# Revit family: ElectricalFixture_WiringAccessories_Hager_Sollysta_RaisedDecorative50ADoublePoleSwitches
name_source: partatom
category: Electrical Fixtures
revit_build: Autodesk Revit 2015 (Build: 20160512_1515(x64)
units: mm (PartAtom-declared; Revit-internal decimal feet)

## types (7) — shared parameters
CE Approval = Yes
Default Elevation = 1219.2 mm  [stored 4 ft]
Design Country = China
Distance From Centre = 22.4 mm
Distance From Edge = 63.6 mm
Double = No
Expected Life = 25 years
Extrusion From Wall = 11.9 mm  [stored 0.039042 ft]
Frequency = 50/60Hz
Gross Weight kg = 0.165
LED Indicator Switch = Yes
Manufacturer = Hager
Manufacturer Country = United Kingdom
Manufacturer Website = http://www.hager.co.uk
Overall Depth = 21.9 mm
Overall Height = 86 mm  [stored 0.282152 ft]
Overall Length = 86 mm  [stored 0.282152 ft]
Overall Width = 86 mm  [stored 0.282152 ft]
Packaging Recyclable = Yes
Product Family = Decorative50ADoublePoleSwitches
Product Group = WiringAccessories
Product Literature = http://www.hager.co.uk
Product Range = Sollysta
Product URL = http://www.hager.co.uk
Reference Standard = BS 1363-2
Shape = Rectangular
Shipping Weight kg = 0.188
Single = Yes
Supply Phase = 1
Switch = Yes
Type = ElectricalFixture
Voltage (Volts) = 230V/240V

## per-type parameters (varying)
| type | Colour | Description | EAN Code | Features | Finish | Material | Name | Technical Description |
| WRDP50NPSW | PolishedSteel | 50ADoublePoleSwitch1GangwithLEDIndicatorPolishedSteelWhiteInsert | 5015654741792 | 50ADoublePoleSwitch1GangwithLEDIndicatorPolishedSteelWhiteInsert | Polished | Hager_PolishedSteel | 50ADoublePoleSwitch1GangwithLEDIndicatorPolishedSteelWhiteInsert | 50ADoublePoleSwitch1GangwithLEDIndicatorPolishedSteelWhiteInsert |
| WRDP50NBSW | BrushedSteel | 50ADoublePoleSwitch1GangwithLEDIndicatorBrushedSteelWhiteInsert | 5015654741839 | 50ADoublePoleSwitch1GangwithLEDIndicatorBrushedSteelWhiteInsert | Brushed | Hager_BrushedSteel | 50ADoublePoleSwitch1GangwithLEDIndicatorBrushedSteelWhiteInsert | 50ADoublePoleSwitch1GangwithLEDIndicatorBrushedSteelWhiteInsert |
| WRDP50NPBW | PolishedBrass | 50ADoublePoleSwitch1GangwithLEDIndicatorPolishedBrassWhiteInsert | 5015654741877 | 50ADoublePoleSwitch1GangwithLEDIndicatorPolishedBrassWhiteInsert | Polished | Hager_PolishedBrass | 50ADoublePoleSwitch1GangwithLEDIndicatorPolishedBrassWhiteInsert | 50ADoublePoleSwitch1GangwithLEDIndicatorPolishedBrassWhiteInsert |
| WRDP50NBSB | BrushedSteel | 50ADoublePoleSwitch1GangwithLEDIndicatorBrushedSteelBlackInsert | 5015654741853 | 50ADoublePoleSwitch1GangwithLEDIndicatorBrushedSteelBlackInsert | Brushed | Hager_BrushedSteel | 50ADoublePoleSwitch1GangwithLEDIndicatorBrushedSteelBlackInsert | 50ADoublePoleSwitch1GangwithLEDIndicatorBrushedSteelBlackInsert |
| WRDP50NPBB | PolishedBrass | 50ADoublePoleSwitch1GangwithLEDIndicatorPolishedBrassBlackInsert | 5015654741891 | 50ADoublePoleSwitch1GangwithLEDIndicatorPolishedBrassBlackInsert | Polished | Hager_PolishedBrass | 50ADoublePoleSwitch1GangwithLEDIndicatorPolishedBrassBlackInsert | 50ADoublePoleSwitch1GangwithLEDIndicatorPolishedBrassBlackInsert |
| WRDP50NPSB | PolishedSteel | 50ADoublePoleSwitch1GangwithLEDIndicatorPolishedSteelBlackInsert | 5015654741815 | 50ADoublePoleSwitch1GangwithLEDIndicatorPolishedSteelBlackInsert | Polished | Hager_PolishedSteel | 50ADoublePoleSwitch1GangwithLEDIndicatorPolishedSteelBlackInsert | 50ADoublePoleSwitch1GangwithLEDIndicatorPolishedSteelBlackInsert |
| WRDP50NBNB | BlackNickel | 50ADoublePoleSwitch1GangwithLEDIndicatorBlackNickelBlackInsert | 5015654741914 | 50ADoublePoleSwitch1GangwithLEDIndicatorBlackNickelBlackInsert | BlackNickel | Hager_BlackNickel | 50ADoublePoleSwitch1GangwithLEDIndicatorBlackNickelBlackInsert | 50ADoublePoleSwitch1GangwithLEDIndicatorBlackNickelBlackInsert |

note: column(s) folded — value = type name in every type: Product Model Number, Unique Reference

note: [stored X ft] marks values corroborated as IEEE doubles in the binary element streams (Revit-internal decimal feet)

## geometry (parser evidence)
native form markers: Blend x4, Sweep x6
no freeform markers — native parametric forms only
